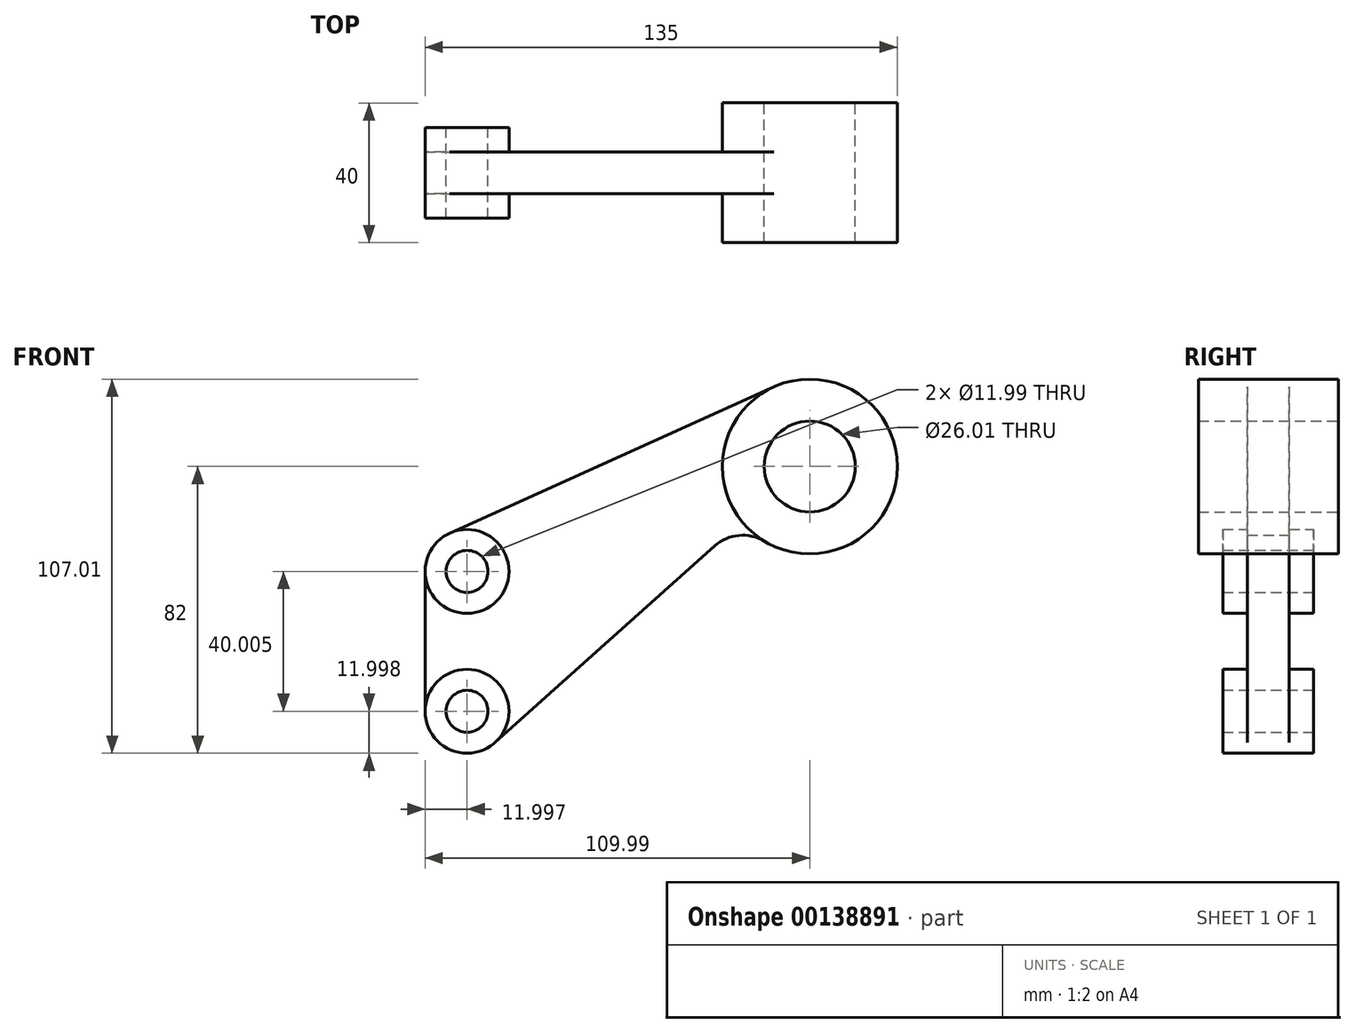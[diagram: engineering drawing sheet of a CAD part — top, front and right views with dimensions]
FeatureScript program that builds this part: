
annotation { "Feature Type Name" : "Feature", "Feature Type Description" : "" }
export const myFeature = defineFeature(function(context is Context, id is Id, definition is map)
    precondition{}
    {
        {
            var Q0;
            Q0=qCreatedBy(makeId("Front.planeOp"),FACE);
            var sketch = newSketch(context, id + "F0", { "sketchPlane" : qUnion([Q0])});
            skCircle(sketch, "E0", {"center": v(0, 0) * mm, "radius": 25 * mm});
            skCircle(sketch, "E1", {"center": v(0, 0) * mm, "radius": 13 * mm});
            skCircle(sketch, "E2", {"center": v(-98, -30) * mm, "radius": 12 * mm});
            skCircle(sketch, "E3", {"center": v(-98, -70) * mm, "radius": 12 * mm});
            skCircle(sketch, "E4", {"center": v(-98, -30) * mm, "radius": 6 * mm});
            skCircle(sketch, "E5", {"center": v(-98, -70) * mm, "radius": 6 * mm});
            skLineSegment(sketch, "E6", {"start": v(-110, -30) * mm, "end": v(-110, -70) * mm});
            skLineSegment(sketch, "E7", {"start": v(-102.93, -19.06) * mm, "end": v(-10.3, 22.79) * mm});
            skLineSegment(sketch, "E8", {"start": v(-27.15, -22.71) * mm, "end": v(-90, -78.95) * mm});
            skPoint(sketch, "E9", {"position": v(-19.16, -31.65) * mm});
            skArc(sketch, "E10", {"start": v(-12.95, -21.4) * mm, "mid": v(-20.27, -19.71) * mm, "end": v(-27.15, -22.71) * mm});
            skSolve(sketch);
        }
        {
            var Q0;
            {var subQ0=sQuery(id+"F0.wireOp",EDGE,"E6");Q0=makeQuery(id+"F0.imprint","IMPRINT",FACE,{"disambiguationData":[TD([[makeQuery(id+"F0.imprint","IMPRINT",EDGE,{"derivedFrom":subQ0}),1.0]])]});}
            extrude(context, id + "F1", {"entities" : qUnion([Q0]), "endBound" : BoundingType.SYMMETRIC, "depth" : 12 * mm});
        }
        {
            var Q0;
            Q0=makeQuery(id+"F0.imprint","IMPRINT",FACE,{"disambiguationData":[TD([[makeQuery(id+"F0.imprint","IMPRINT",EDGE,{"derivedFrom":sQuery(id+"F0.wireOp",EDGE,"E5")}),-1.0]])]});
            var Q1;
            Q1=makeQuery(id+"F0.imprint","IMPRINT",FACE,{"disambiguationData":[TD([[makeQuery(id+"F0.imprint","IMPRINT",EDGE,{"derivedFrom":sQuery(id+"F0.wireOp",EDGE,"E4")}),-1.0]])]});
            extrude(context, id + "F2", {"entities" : qUnion([Q0, Q1]), "operationType" : NewBodyOperationType.ADD, "endBound" : BoundingType.SYMMETRIC, "depth" : 26 * mm});
        }
        {
            var Q0;
            Q0=makeQuery(id+"F0.imprint","IMPRINT",FACE,{"disambiguationData":[TD([[makeQuery(id+"F0.imprint","IMPRINT",EDGE,{"derivedFrom":sQuery(id+"F0.wireOp",EDGE,"E1")}),-1.0]])]});
            extrude(context, id + "F3", {"entities" : qUnion([Q0]), "operationType" : NewBodyOperationType.ADD, "endBound" : BoundingType.SYMMETRIC, "depth" : 40 * mm});
        }
    });
